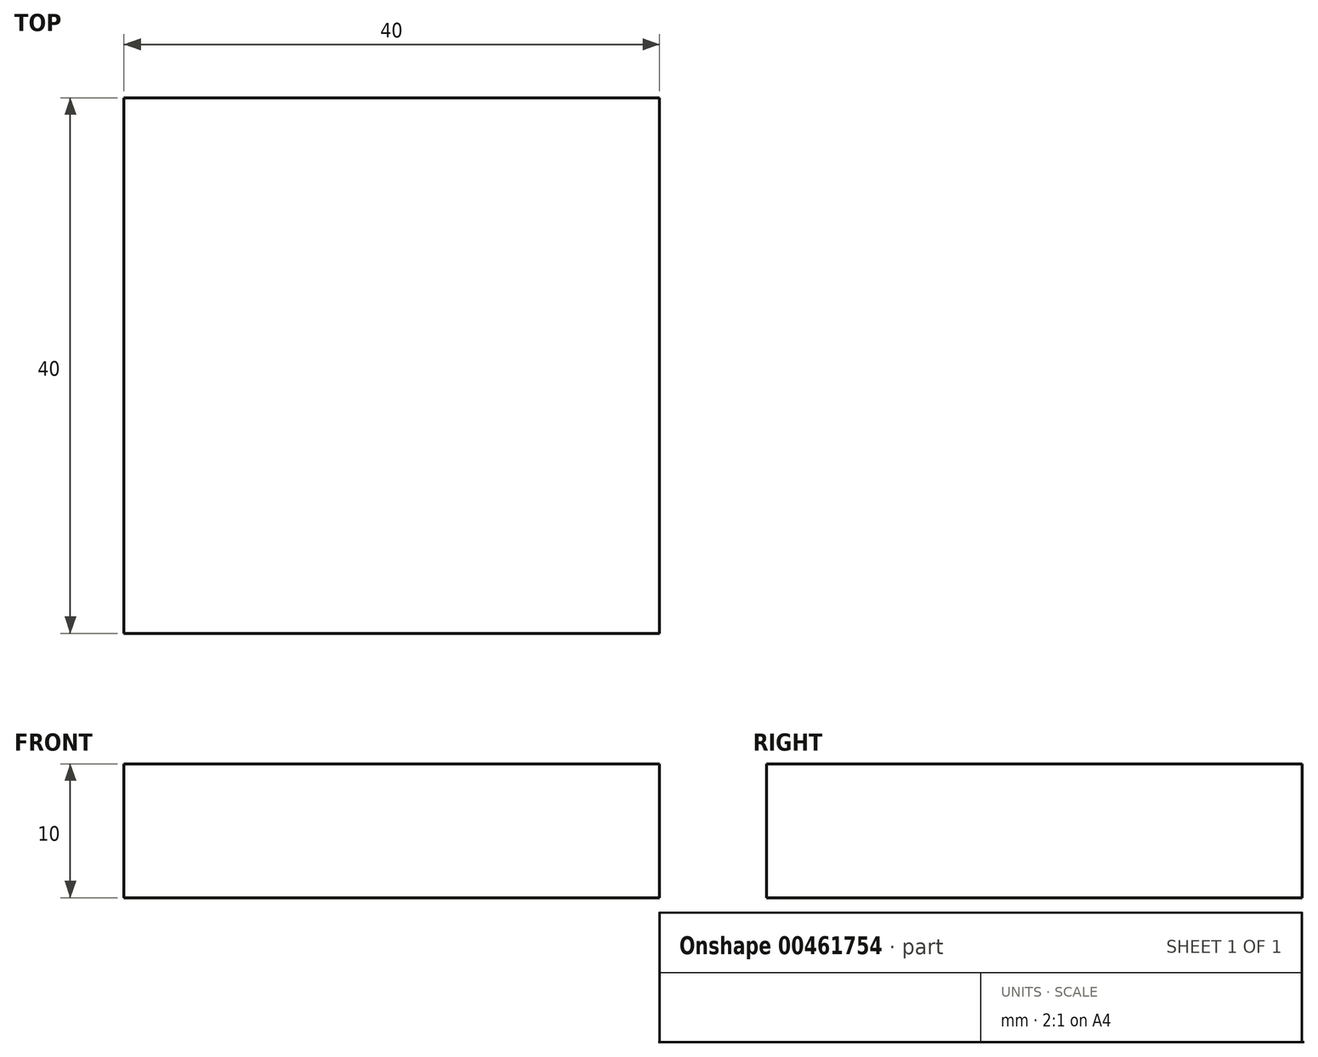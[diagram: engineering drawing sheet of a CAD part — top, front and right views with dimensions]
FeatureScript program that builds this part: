
annotation { "Feature Type Name" : "Feature", "Feature Type Description" : "" }
export const myFeature = defineFeature(function(context is Context, id is Id, definition is map)
    precondition{}
    {
        {
            var Q0;
            Q0=qCreatedBy(makeId("Top.planeOp"),FACE);
            var sketch = newSketch(context, id + "F0", { "sketchPlane" : qUnion([Q0])});
            skLineSegment(sketch, "E0.bottom", {"start": v(20, -20) * mm, "end": v(-20, -20) * mm});
            skLineSegment(sketch, "E0.top", {"start": v(20, 20) * mm, "end": v(-20, 20) * mm});
            skLineSegment(sketch, "E0.left", {"start": v(20, -20) * mm, "end": v(20, 20) * mm});
            skLineSegment(sketch, "E0.right", {"start": v(-20, -20) * mm, "end": v(-20, 20) * mm});
            skPoint(sketch, "E0.middle", {"position": v(0, 0) * mm});
            skSolve(sketch);
        }
        {
            var Q0;
            Q0 = qSketchRegion(id + "F0", true);
            extrude(context, id + "F1", {"entities" : qUnion([Q0]), "depth" : 10 * mm, "offsetDistance" : 25 * mm});
        }
    });
